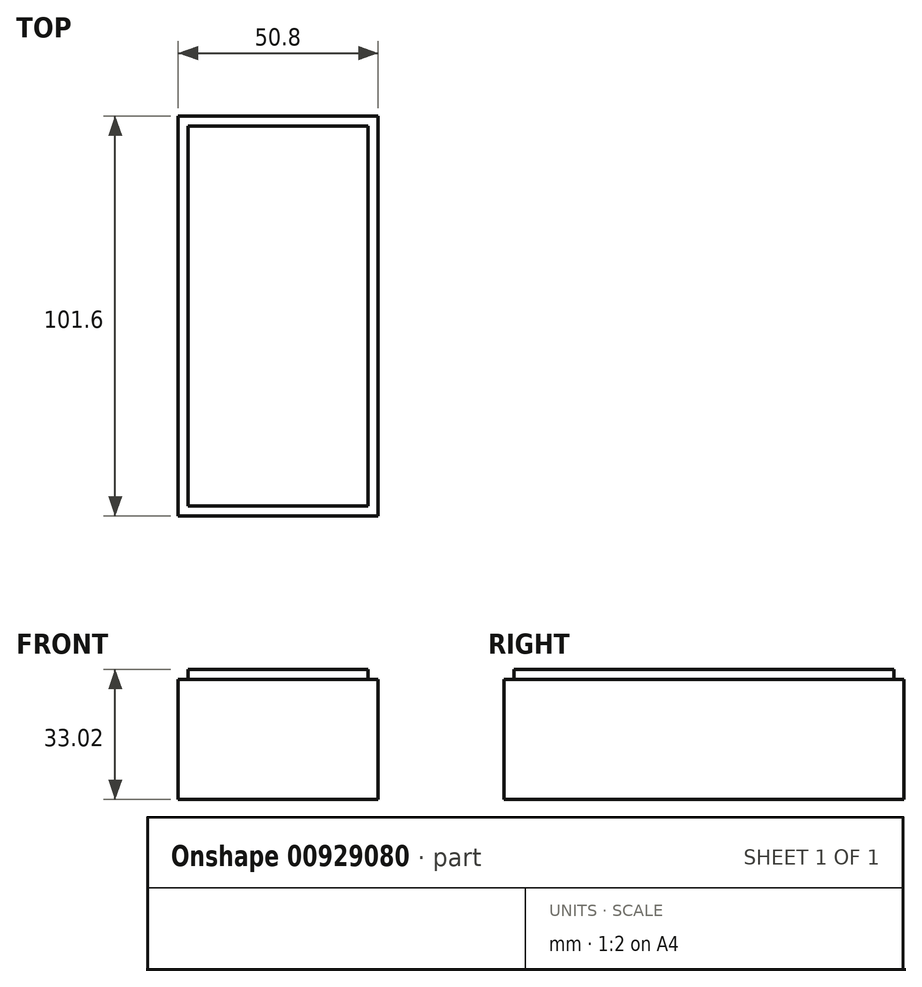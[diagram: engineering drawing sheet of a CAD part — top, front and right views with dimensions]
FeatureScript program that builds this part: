
annotation { "Feature Type Name" : "Feature", "Feature Type Description" : "" }
export const myFeature = defineFeature(function(context is Context, id is Id, definition is map)
    precondition{}
    {
        {
            var Q0;
            Q0=qCreatedBy(makeId("Top.planeOp"),FACE);
            var sketch = newSketch(context, id + "F0", { "sketchPlane" : qUnion([Q0])});
            skLineSegment(sketch, "E0.bottom", {"start": v(-25.4, 50.8) * mm, "end": v(25.4, 50.8) * mm});
            skLineSegment(sketch, "E0.top", {"start": v(-25.4, -50.8) * mm, "end": v(25.4, -50.8) * mm});
            skLineSegment(sketch, "E0.left", {"start": v(-25.4, 50.8) * mm, "end": v(-25.4, -50.8) * mm});
            skLineSegment(sketch, "E0.right", {"start": v(25.4, 50.8) * mm, "end": v(25.4, -50.8) * mm});
            skLineSegment(sketch, "E1", {"start": v(-25.4, 0) * mm, "end": v(0, 0) * mm, "construction": true});
            skLineSegment(sketch, "E2", {"start": v(0, 0) * mm, "end": v(25.4, 0) * mm, "construction": true});
            skSolve(sketch);
        }
        {
            var Q0;
            Q0 = qSketchRegion(id + "F0", true);
            extrude(context, id + "F1", {"entities" : qUnion([Q0]), "depth" : 30.48 * mm, "offsetDistance" : 25.4 * mm});
        }
        {
            var Q0;
            Q0=makeQuery(id+"F1.opExtrude","CAP_FACE",FACE,{"disambiguationData":[OSD([sQuery(id+"F0.wireOp",EDGE,"E0.bottom"),sQuery(id+"F0.wireOp",EDGE,"E0.top"),sQuery(id+"F0.wireOp",EDGE,"E0.left"),sQuery(id+"F0.wireOp",EDGE,"E0.right")])],"isStart":false});
            var sketch = newSketch(context, id + "F2", { "sketchPlane" : qUnion([Q0])});
            skLineSegment(sketch, "E3.bottom", {"start": v(-22.86, 48.26) * mm, "end": v(22.86, 48.26) * mm});
            skLineSegment(sketch, "E3.top", {"start": v(-22.86, -48.26) * mm, "end": v(22.86, -48.26) * mm});
            skLineSegment(sketch, "E3.left", {"start": v(-22.86, 48.26) * mm, "end": v(-22.86, -48.26) * mm});
            skLineSegment(sketch, "E3.right", {"start": v(22.86, 48.26) * mm, "end": v(22.86, -48.26) * mm});
            skLineSegment(sketch, "E4", {"start": v(22.86, 48.26) * mm, "end": v(22.86, 50.8) * mm, "construction": true});
            skLineSegment(sketch, "E5", {"start": v(22.86, 50.8) * mm, "end": v(22.86, 48.26) * mm, "construction": true});
            skLineSegment(sketch, "E6", {"start": v(25.4, 48.26) * mm, "end": v(22.86, 48.26) * mm, "construction": true});
            skLineSegment(sketch, "E7", {"start": v(-22.86, -48.26) * mm, "end": v(-22.86, -50.8) * mm, "construction": true});
            skLineSegment(sketch, "E8", {"start": v(-22.86, -48.26) * mm, "end": v(-25.4, -48.26) * mm, "construction": true});
            skSolve(sketch);
        }
        {
            var Q0;
            Q0 = qSketchRegion(id + "F2", true);
            extrude(context, id + "F3", {"entities" : qUnion([Q0]), "operationType" : NewBodyOperationType.ADD, "depth" : 2.54 * mm, "offsetDistance" : 25.4 * mm});
        }
    });
